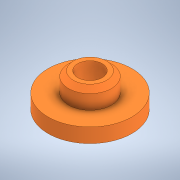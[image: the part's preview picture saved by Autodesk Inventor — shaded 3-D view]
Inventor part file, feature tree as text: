
AUTODESK INVENTOR PART (.ipt)
format: ipt  version: 2022 (Build 260153000, 153)  size: 277,504 bytes
history: native  units: mm
features: extrude x2, sketch x2, chamfer x1
ambient origin geometry x8: Origin, YZ Plane, XZ Plane, XY Plane, X Axis, Y Axis, Z Axis, Center Point
bodies: Solid1 (feature_tree)
feature tree (5):
  extrude  "Extrusion1"  Depth=8.0mm
  chamfer  "Chamfer1"  Distance=8.0mm
  extrude  "Extrusion2"  Depth=6.0mm
  sketch  "Sketch1"  dims[d0=10.2mm d1=17.9mm d2=8.0mm d3=0.0mm]
  sketch  "Sketch2"  dims[d4=2.0mm d5=2.0mm d6=45.0deg d7=35.0mm d8=6.0mm d9=0.0mm]
